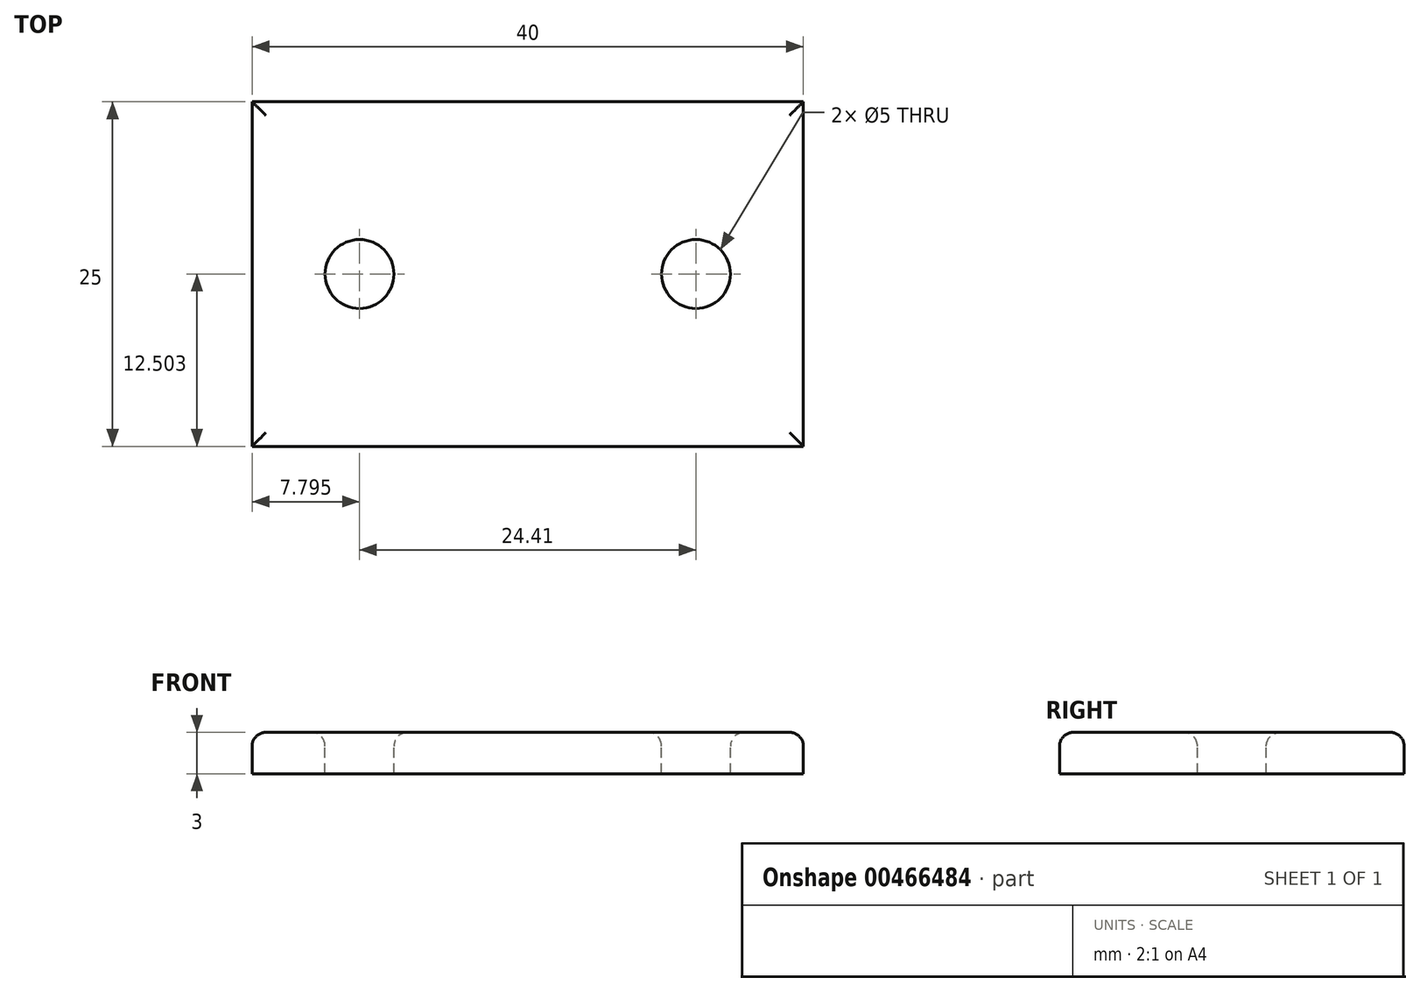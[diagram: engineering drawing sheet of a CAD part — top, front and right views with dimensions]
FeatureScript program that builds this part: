
annotation { "Feature Type Name" : "Feature", "Feature Type Description" : "" }
export const myFeature = defineFeature(function(context is Context, id is Id, definition is map)
    precondition{}
    {
        {
            var Q0;
            Q0=qCreatedBy(makeId("Top.planeOp"),FACE);
            var sketch = newSketch(context, id + "F0", { "sketchPlane" : qUnion([Q0])});
            skLineSegment(sketch, "E0.bottom", {"start": v(-20, 44.61) * mm, "end": v(20, 44.61) * mm});
            skLineSegment(sketch, "E0.top", {"start": v(-20, 19.61) * mm, "end": v(20, 19.61) * mm});
            skLineSegment(sketch, "E0.left", {"start": v(-20, 44.61) * mm, "end": v(-20, 19.61) * mm});
            skLineSegment(sketch, "E0.right", {"start": v(20, 44.61) * mm, "end": v(20, 19.61) * mm});
            skSolve(sketch);
        }
        {
            var Q0;
            Q0=makeQuery(id+"F0.imprint","IMPRINT",FACE,{"disambiguationData":[TD([[makeQuery(id+"F0.imprint","IMPRINT",EDGE,{"derivedFrom":sQuery(id+"F0.wireOp",EDGE,"E0.bottom")}),-1.0]])]});
            extrude(context, id + "F1", {"entities" : qUnion([Q0]), "depth" : 3 * mm});
        }
        {
            var Q0;
            Q0=qCreatedBy(makeId("Top.planeOp"),FACE);
            cPlane(context, id + "F2", {"entities" : qUnion([Q0]), "cplaneType" : CPlaneType.OFFSET, "offset" : 5 * mm, "width" : 150 * mm, "height" : 150 * mm});
        }
        {
            var Q0;
            Q0=qCreatedBy(id+"F2.planeOp",FACE);
            var sketch = newSketch(context, id + "F3", { "sketchPlane" : qUnion([Q0])});
            skCircle(sketch, "E1", {"center": v(-12.2, 32.11) * mm, "radius": 2.5 * mm});
            skCircle(sketch, "E2", {"center": v(12.2, 32.11) * mm, "radius": 2.5 * mm});
            skSolve(sketch);
        }
        {
            var Q0;
            Q0=sQuery(id+"F3.wireOp",VERTEX,"E1.center");
            var Q1;
            Q1=sQuery(id+"F3.wireOp",VERTEX,"E2.center");
            var Q2;
            Q2=makeQuery(id+"F1.opExtrude","SWEPT_BODY",BODY,{"disambiguationData":[OSD([sQuery(id+"F0.wireOp",EDGE,"E0.bottom"),sQuery(id+"F0.wireOp",EDGE,"E0.top"),sQuery(id+"F0.wireOp",EDGE,"E0.left"),sQuery(id+"F0.wireOp",EDGE,"E0.right")])]});
            hole(context, id + "F4", {"style" : HoleStyle.SIMPLE, "endStyle" : HoleEndStyle.THROUGH, "holeDiameter" : 5 * mm, "isTappedThrough" : true, "tappedDepth" : 12 * mm, "tapClearance" : 3, "locations" : qUnion([Q0, Q1]), "scope" : qUnion([Q2])});
        }
        {
            var Q0;
            Q0=makeQuery(id+"F1.opExtrude","CAP_FACE",FACE,{"disambiguationData":[OSD([sQuery(id+"F0.wireOp",EDGE,"E0.bottom"),sQuery(id+"F0.wireOp",EDGE,"E0.top"),sQuery(id+"F0.wireOp",EDGE,"E0.left"),sQuery(id+"F0.wireOp",EDGE,"E0.right")])],"isStart":false});
            fillet(context, id + "F5", {"entities" : qUnion([Q0]), "radius" : 1 * mm, "tangentPropagation" : true, "allowEdgeOverflow" : false});
        }
    });
